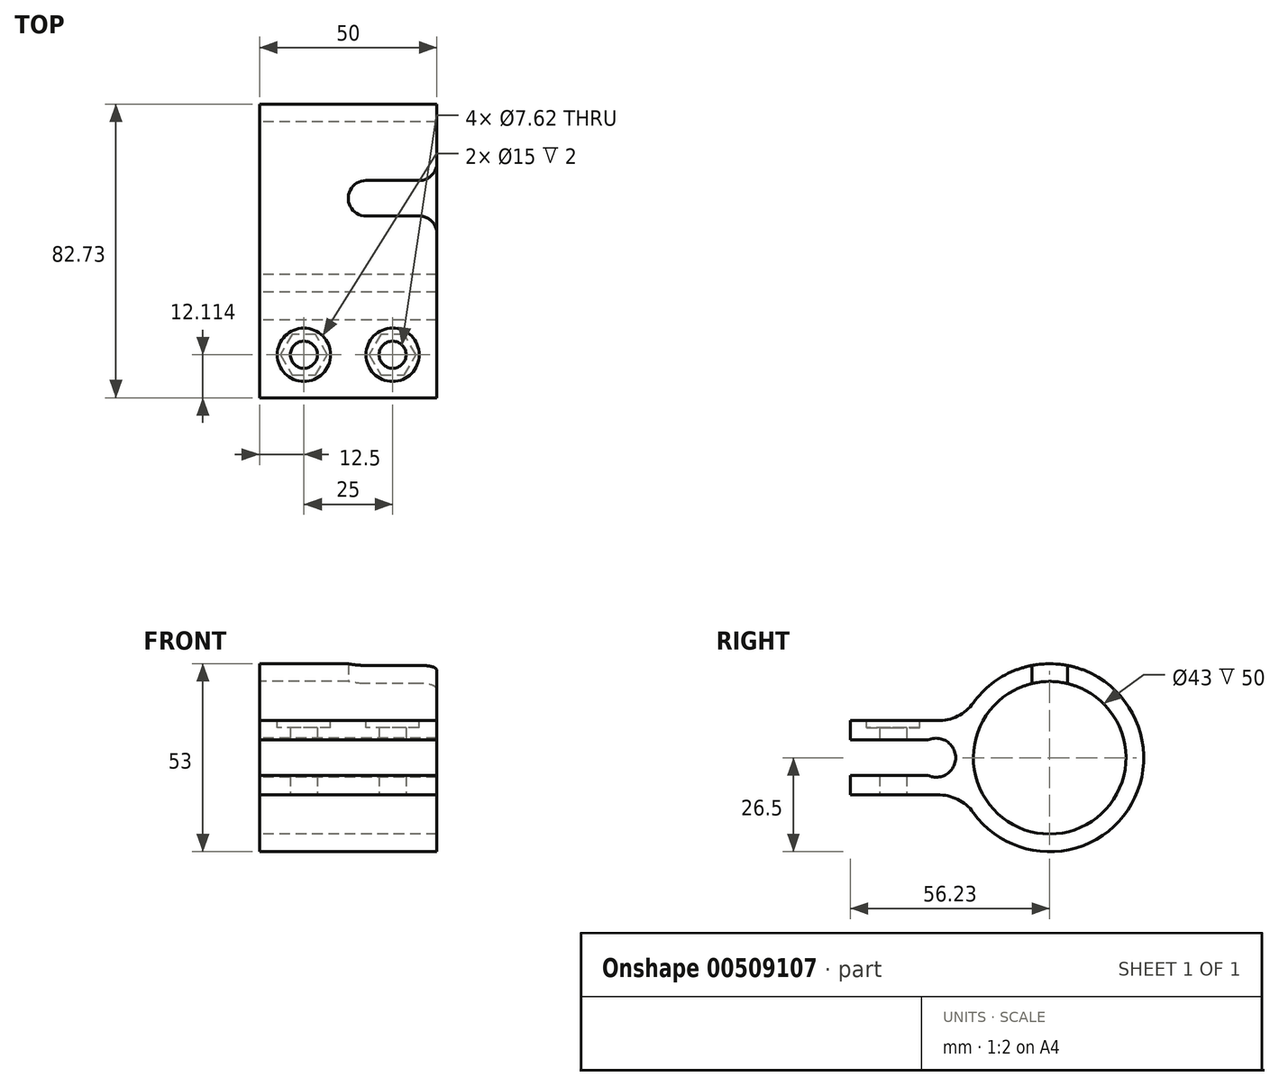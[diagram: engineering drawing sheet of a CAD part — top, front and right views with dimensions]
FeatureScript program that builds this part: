
annotation { "Feature Type Name" : "Feature", "Feature Type Description" : "" }
export const myFeature = defineFeature(function(context is Context, id is Id, definition is map)
    precondition{}
    {
        {
            var Q0;
            Q0=qCreatedBy(makeId("Right.planeOp"),FACE);
            var sketch = newSketch(context, id + "F0", { "sketchPlane" : qUnion([Q0])});
            skCircle(sketch, "E0", {"center": v(0, 0) * mm, "radius": 5.5 * mm});
            skCircle(sketch, "E1", {"center": v(0, 0) * mm, "radius": 10.5 * mm});
            skLineSegment(sketch, "E2.bottom", {"start": v(-2.3, 5) * mm, "end": v(-9.23, 5) * mm});
            skLineSegment(sketch, "E2.top", {"start": v(-2.3, -5) * mm, "end": v(-9.23, -5) * mm});
            skLineSegment(sketch, "E2.left", {"start": v(-2.3, 5) * mm, "end": v(-2.3, -5) * mm, "construction": true});
            skLineSegment(sketch, "E2.right", {"start": v(-9.23, 5) * mm, "end": v(-9.23, -5) * mm, "construction": true});
            skLineSegment(sketch, "E3", {"start": v(0, 10.5) * mm, "end": v(-24.23, 10.5) * mm});
            skLineSegment(sketch, "E4", {"start": v(-24.23, 10.5) * mm, "end": v(-24.23, 5) * mm});
            skLineSegment(sketch, "E5", {"start": v(-24.23, 5) * mm, "end": v(-9.23, 5) * mm});
            skLineSegment(sketch, "E6", {"start": v(0, 0) * mm, "end": v(-31.53, 0) * mm, "construction": true});
            skPoint(sketch, "E6.endSnap0", {"position": v(-2.3, 0) * mm});
            skLineSegment(sketch, "E7.MirrorCS", {"start": v(0, -10.5) * mm, "end": v(-24.23, -10.5) * mm});
            skLineSegment(sketch, "E8.MirrorCS", {"start": v(-24.23, -10.5) * mm, "end": v(-24.23, -5) * mm});
            skLineSegment(sketch, "E9.MirrorCS", {"start": v(-24.23, -5) * mm, "end": v(-9.23, -5) * mm});
            skSolve(sketch);
        }
        {
            var Q0;
            {var subQ2=sQuery(id+"F0.wireOp",EDGE,"E3");Q0=makeQuery(id+"F0.imprint","IMPRINT",FACE,{"disambiguationData":[TD([[makeQuery(id+"F0.imprint","IMPRINT",EDGE,{"derivedFrom":subQ2}),1.0]])]});}
            var Q1;
            {var subQ4=sQuery(id+"F0.wireOp",EDGE,"E2.bottom");Q1=makeQuery(id+"F0.imprint","IMPRINT",FACE,{"disambiguationData":[TD([[makeQuery(id+"F0.imprint","IMPRINT",EDGE,{"derivedFrom":subQ4}),-1.0]])]});}
            var Q2;
            {var subQ2=sQuery(id+"F0.wireOp",EDGE,"E7.MirrorCS");Q2=makeQuery(id+"F0.imprint","IMPRINT",FACE,{"disambiguationData":[TD([[makeQuery(id+"F0.imprint","IMPRINT",EDGE,{"derivedFrom":subQ2}),-1.0]])]});}
            extrude(context, id + "F1", {"entities" : qUnion([Q0, Q1, Q2]), "endBound" : BoundingType.SYMMETRIC, "depth" : 50 * mm});
        }
        {
            var Q0;
            Q0=makeQuery(id+"F1.opExtrude","SWEPT_FACE",FACE,{"disambiguationData":[OSD([sQuery(id+"F0.wireOp",EDGE,"E7.MirrorCS")])]});
            var sketch = newSketch(context, id + "F2", { "sketchPlane" : qUnion([Q0])});
            skCircle(sketch, "E10.cCircle", {"center": v(12.5, 12.12) * mm, "radius": 5.75 * mm, "construction": true});
            skLineSegment(sketch, "E10.0", {"start": v(15.82, 17.87) * mm, "end": v(19.14, 12.12) * mm});
            skLineSegment(sketch, "E10.1", {"start": v(19.14, 12.12) * mm, "end": v(15.82, 6.37) * mm});
            skLineSegment(sketch, "E10.2", {"start": v(15.82, 6.37) * mm, "end": v(9.18, 6.37) * mm});
            skLineSegment(sketch, "E10.3", {"start": v(9.18, 6.37) * mm, "end": v(5.86, 12.12) * mm});
            skLineSegment(sketch, "E10.4", {"start": v(5.86, 12.12) * mm, "end": v(9.18, 17.87) * mm});
            skLineSegment(sketch, "E10.5", {"start": v(9.18, 17.87) * mm, "end": v(15.82, 17.87) * mm});
            skPoint(sketch, "E10.0.midPoint", {"position": v(17.48, 15) * mm});
            skCircle(sketch, "E11.cCircle", {"center": v(-12.5, 12.12) * mm, "radius": 5.75 * mm, "construction": true});
            skLineSegment(sketch, "E11.0", {"start": v(-9.18, 6.37) * mm, "end": v(-15.82, 6.37) * mm});
            skLineSegment(sketch, "E11.1", {"start": v(-15.82, 6.37) * mm, "end": v(-19.14, 12.12) * mm});
            skLineSegment(sketch, "E11.2", {"start": v(-19.14, 12.12) * mm, "end": v(-15.82, 17.87) * mm});
            skLineSegment(sketch, "E11.3", {"start": v(-15.82, 17.87) * mm, "end": v(-9.18, 17.87) * mm});
            skLineSegment(sketch, "E11.4", {"start": v(-9.18, 17.87) * mm, "end": v(-5.86, 12.12) * mm});
            skLineSegment(sketch, "E11.5", {"start": v(-5.86, 12.12) * mm, "end": v(-9.18, 6.37) * mm});
            skPoint(sketch, "E11.0.midPoint", {"position": v(-12.5, 6.37) * mm});
            skLineSegment(sketch, "E12", {"start": v(12.5, 12.12) * mm, "end": v(-12.5, 12.12) * mm, "construction": true});
            skLineSegment(sketch, "E13", {"start": v(0, 0) * mm, "end": v(0, 12.12) * mm, "construction": true});
            skSolve(sketch);
        }
        {
            var Q0;
            Q0 = qSketchRegion(id + "F2", true);
            extrude(context, id + "F3", {"entities" : qUnion([Q0]), "operationType" : NewBodyOperationType.REMOVE, "oppositeDirection" : true, "depth" : 5 / 812.8 * mm});
        }
        {
            var Q0;
            Q0=makeQuery(id+"F2.imprint","IMPRINT",FACE,{"disambiguationData":[TD([[makeQuery(id+"F2.imprint","IMPRINT",EDGE,{"derivedFrom":sQuery(id+"F2.wireOp",EDGE,"E10.0")}),-1.0]])]});
            var sketch = newSketch(context, id + "F4", { "sketchPlane" : qUnion([Q0])});
            skCircle(sketch, "E14", {"center": v(12.5, 12.12) * mm, "radius": 3.81 * mm});
            skCircle(sketch, "E15", {"center": v(-12.5, 12.12) * mm, "radius": 3.81 * mm});
            skSolve(sketch);
        }
        {
            var Q0;
            Q0 = qSketchRegion(id + "F4", true);
            extrude(context, id + "F5", {"entities" : qUnion([Q0]), "operationType" : NewBodyOperationType.REMOVE, "endBound" : BoundingType.THROUGH_ALL, "oppositeDirection" : true, "depth" : 25 * mm});
        }
        {
            var Q0;
            Q0=makeQuery(id+"F1.opExtrude","SWEPT_FACE",FACE,{"disambiguationData":[OSD([sQuery(id+"F0.wireOp",EDGE,"E3")])]});
            var sketch = newSketch(context, id + "F6", { "sketchPlane" : qUnion([Q0])});
            skCircle(sketch, "E16", {"center": v(-12.5, -12.12) * mm, "radius": 7.5 * mm});
            skCircle(sketch, "E17", {"center": v(12.5, -12.12) * mm, "radius": 7.5 * mm});
            skSolve(sketch);
        }
        {
            var Q0;
            Q0 = qSketchRegion(id + "F6", true);
            extrude(context, id + "F7", {"entities" : qUnion([Q0]), "operationType" : NewBodyOperationType.REMOVE, "oppositeDirection" : true, "depth" : 2 * mm});
        }
        {
            var Q0;
            Q0=qCreatedBy(makeId("Right.planeOp"),FACE);
            var sketch = newSketch(context, id + "F8", { "sketchPlane" : qUnion([Q0])});
            skCircle(sketch, "E18", {"center": v(32, 0) * mm, "radius": 21.5 * mm});
            skCircle(sketch, "E19", {"center": v(32, 0) * mm, "radius": 26.5 * mm});
            skSolve(sketch);
        }
        {
            var Q0;
            Q0 = qSketchRegion(id + "F8", true);
            extrude(context, id + "F9", {"entities" : qUnion([Q0]), "operationType" : NewBodyOperationType.ADD, "endBound" : BoundingType.SYMMETRIC, "depth" : 50 * mm});
        }
        {
            var Q0;
            Q0=qCreatedBy(makeId("Top.planeOp"),FACE);
            var sketch = newSketch(context, id + "F10", { "sketchPlane" : qUnion([Q0])});
            skLineSegment(sketch, "E20.bottom", {"start": v(5, 27) * mm, "end": v(46.79, 27) * mm});
            skLineSegment(sketch, "E20.top", {"start": v(5, 37) * mm, "end": v(46.79, 37) * mm});
            skLineSegment(sketch, "E20.left", {"start": v(5, 27) * mm, "end": v(5, 37) * mm});
            skLineSegment(sketch, "E20.right", {"start": v(46.79, 27) * mm, "end": v(46.79, 37) * mm});
            skArc(sketch, "E21", {"start": v(5, 37) * mm, "mid": v(0, 32) * mm, "end": v(5, 27) * mm});
            skSolve(sketch);
        }
        {
            var Q0;
            Q0 = qSketchRegion(id + "F10", true);
            extrude(context, id + "F11", {"entities" : qUnion([Q0]), "operationType" : NewBodyOperationType.REMOVE, "endBound" : BoundingType.THROUGH_ALL, "depth" : 25 * mm});
        }
        {
            var Q0;
            Q0=makeQuery(id+"F11.boolean.opBoolean","INTERSECT",EDGE,{"derivedFrom":[makeQuery(id+"F9.boolean.opBoolean","MERGE",FACE,{"derivedFrom":[makeQuery(id+"F1.opExtrude","CAP_FACE",FACE,{"disambiguationData":[OSD([sQuery(id+"F0.wireOp",EDGE,"E0"),sQuery(id+"F0.wireOp",EDGE,"E1"),sQuery(id+"F0.wireOp",EDGE,"E2.bottom"),sQuery(id+"F0.wireOp",EDGE,"E2.top"),sQuery(id+"F0.wireOp",EDGE,"E3"),sQuery(id+"F0.wireOp",EDGE,"E4"),sQuery(id+"F0.wireOp",EDGE,"E5"),sQuery(id+"F0.wireOp",EDGE,"E7.MirrorCS"),sQuery(id+"F0.wireOp",EDGE,"E8.MirrorCS"),sQuery(id+"F0.wireOp",EDGE,"E9.MirrorCS")])],"isStart":false}),makeQuery(id+"F9.opExtrude","CAP_FACE",FACE,{"disambiguationData":[OSD([sQuery(id+"F8.wireOp",EDGE,"E18"),sQuery(id+"F8.wireOp",EDGE,"E19")])],"isStart":false})]}),makeQuery(id+"F11.opExtrude","SWEPT_FACE",FACE,{"disambiguationData":[OSD([sQuery(id+"F10.wireOp",EDGE,"E20.bottom")])]})]});
            var Q1;
            Q1=makeQuery(id+"F11.boolean.opBoolean","INTERSECT",EDGE,{"derivedFrom":[makeQuery(id+"F9.boolean.opBoolean","MERGE",FACE,{"derivedFrom":[makeQuery(id+"F1.opExtrude","CAP_FACE",FACE,{"disambiguationData":[OSD([sQuery(id+"F0.wireOp",EDGE,"E0"),sQuery(id+"F0.wireOp",EDGE,"E1"),sQuery(id+"F0.wireOp",EDGE,"E2.bottom"),sQuery(id+"F0.wireOp",EDGE,"E2.top"),sQuery(id+"F0.wireOp",EDGE,"E3"),sQuery(id+"F0.wireOp",EDGE,"E4"),sQuery(id+"F0.wireOp",EDGE,"E5"),sQuery(id+"F0.wireOp",EDGE,"E7.MirrorCS"),sQuery(id+"F0.wireOp",EDGE,"E8.MirrorCS"),sQuery(id+"F0.wireOp",EDGE,"E9.MirrorCS")])],"isStart":false}),makeQuery(id+"F9.opExtrude","CAP_FACE",FACE,{"disambiguationData":[OSD([sQuery(id+"F8.wireOp",EDGE,"E18"),sQuery(id+"F8.wireOp",EDGE,"E19")])],"isStart":false})]}),makeQuery(id+"F11.opExtrude","SWEPT_FACE",FACE,{"disambiguationData":[OSD([sQuery(id+"F10.wireOp",EDGE,"E20.top")])]})]});
            fillet(context, id + "F12", {"entities" : qUnion([Q0, Q1]), "radius" : 5 * mm, "tangentPropagation" : true, "allowEdgeOverflow" : false});
        }
        {
            var Q0;
            Q0=makeQuery(id+"F9.boolean.opBoolean","INTERSECT",EDGE,{"disambiguationData":[OD(0.0)],"derivedFrom":[makeQuery(id+"F1.opExtrude","SWEPT_FACE",FACE,{"disambiguationData":[OSD([sQuery(id+"F0.wireOp",EDGE,"E1")])]}),makeQuery(id+"F9.opExtrude","SWEPT_FACE",FACE,{"disambiguationData":[OSD([sQuery(id+"F8.wireOp",EDGE,"E19")])]})]});
            var Q1;
            Q1=makeQuery(id+"F9.boolean.opBoolean","INTERSECT",EDGE,{"disambiguationData":[OD(1.0)],"derivedFrom":[makeQuery(id+"F1.opExtrude","SWEPT_FACE",FACE,{"disambiguationData":[OSD([sQuery(id+"F0.wireOp",EDGE,"E1")])]}),makeQuery(id+"F9.opExtrude","SWEPT_FACE",FACE,{"disambiguationData":[OSD([sQuery(id+"F8.wireOp",EDGE,"E19")])]})]});
            fillet(context, id + "F13", {"entities" : qUnion([Q0, Q1]), "radius" : 12 * mm, "tangentPropagation" : true, "allowEdgeOverflow" : false});
        }
    });
